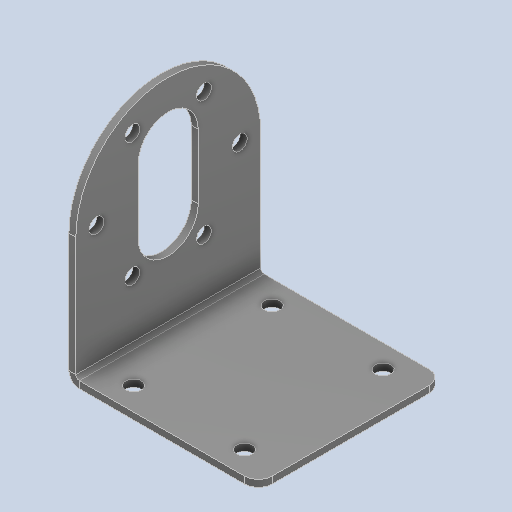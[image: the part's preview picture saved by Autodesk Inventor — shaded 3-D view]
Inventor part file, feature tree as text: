
AUTODESK INVENTOR PART (.ipt)
format: ipt  version: 2023 (Build 270158000, 158)  size: 147,968 bytes
history: mixed  units: in
note: dims shown in document units (in); Inventor stores cm internally (conversion verified against a paired STEP export)
features: fillet x1, imported_body x1
ambient origin geometry x8: Origin, YZ Plane, XZ Plane, XY Plane, X Axis, Y Axis, Z Axis, Center Point
bodies: Solid1 (imported_parasolid)
feature tree (2):
  fillet  "Fillet1"  [1 undecoded]
  imported_body  NMx_Import_Brep_tag  [imported B-rep: ~30 faces, bbox_mm=[41.0, 41.423394, 40.0]]
note: 1 required parameter value undecoded (feature->parameter linkage not recoverable at this tier; creation-order binding heuristic only, values carry confidence <= 0.55)
